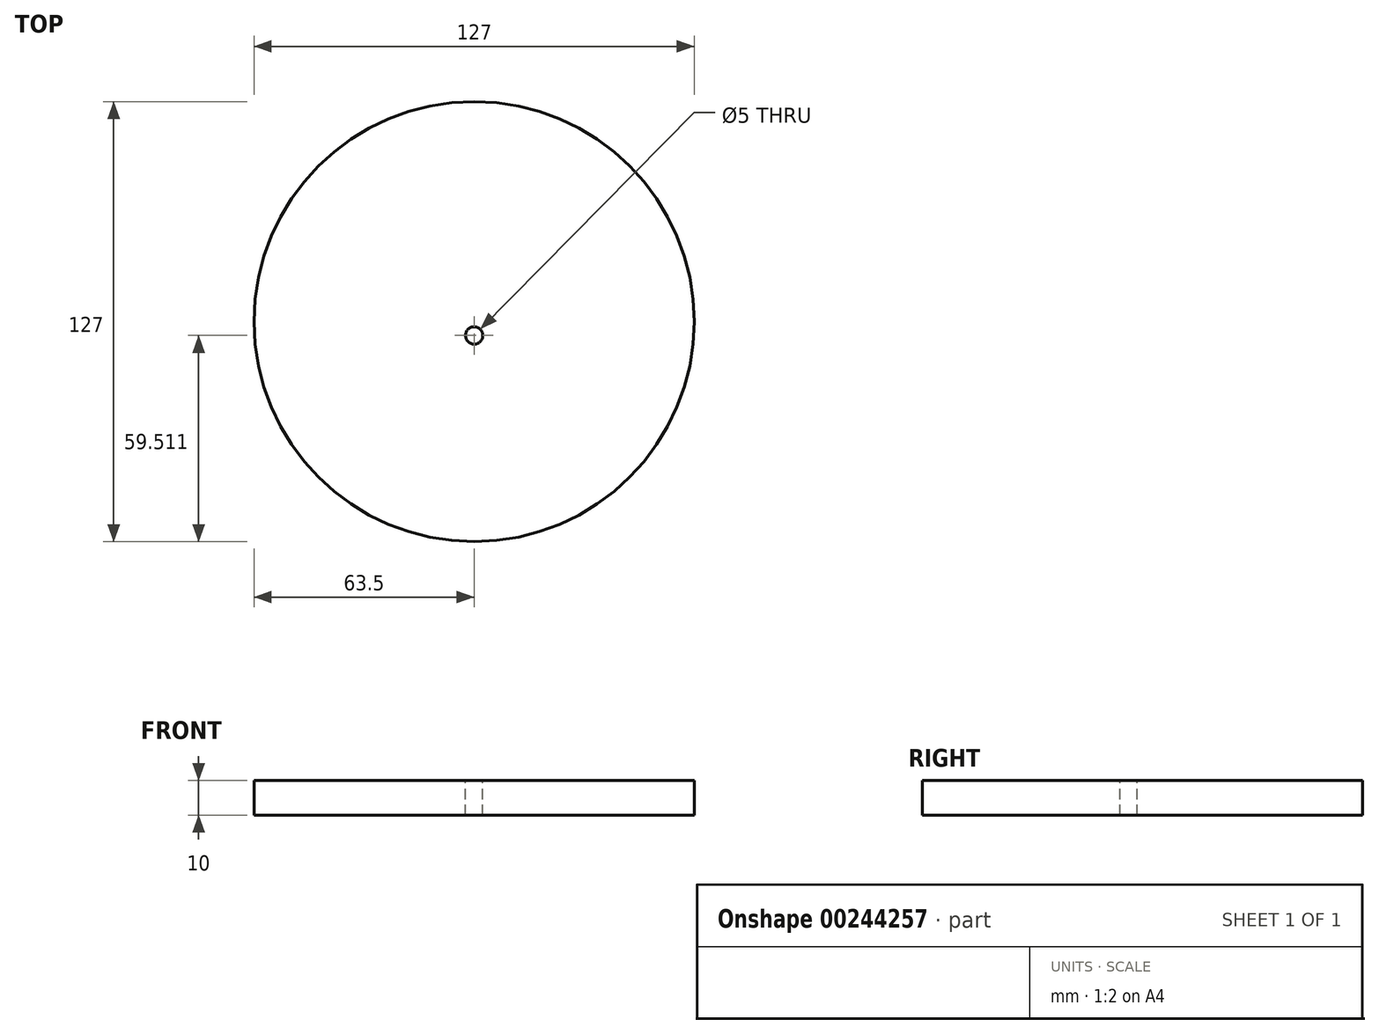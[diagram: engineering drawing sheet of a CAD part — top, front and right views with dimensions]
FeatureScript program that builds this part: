
annotation { "Feature Type Name" : "Feature", "Feature Type Description" : "" }
export const myFeature = defineFeature(function(context is Context, id is Id, definition is map)
    precondition{}
    {
        {
            var Q0;
            Q0=qCreatedBy(makeId("Top.planeOp"),FACE);
            var sketch = newSketch(context, id + "F0", { "sketchPlane" : qUnion([Q0])});
            skCircle(sketch, "E0", {"center": v(0, 0) * mm, "radius": 63.5 * mm});
            skSolve(sketch);
        }
        {
            var Q0;
            Q0=qSketchRegion(id+"F0",true);
            extrude(context, id + "F1", {"entities" : qUnion([Q0]), "depth" : 10 * mm});
        }
        {
            var Q0;
            Q0=makeQuery(id+"F1.opExtrude","CAP_FACE",FACE,{"disambiguationData":[OSD([sQuery(id+"F0.wireOp",EDGE,"E0")])],"isStart":false});
            var sketch = newSketch(context, id + "F2", { "sketchPlane" : qUnion([Q0])});
            skCircle(sketch, "E1", {"center": v(0, -3.99) * mm, "radius": 2.5 * mm});
            skSolve(sketch);
        }
        {
            var Q0;
            Q0=qSketchRegion(id+"F2",true);
            extrude(context, id + "F3", {"entities" : qUnion([Q0]), "operationType" : NewBodyOperationType.REMOVE, "endBound" : BoundingType.THROUGH_ALL, "oppositeDirection" : true, "depth" : 25 * mm});
        }
    });
